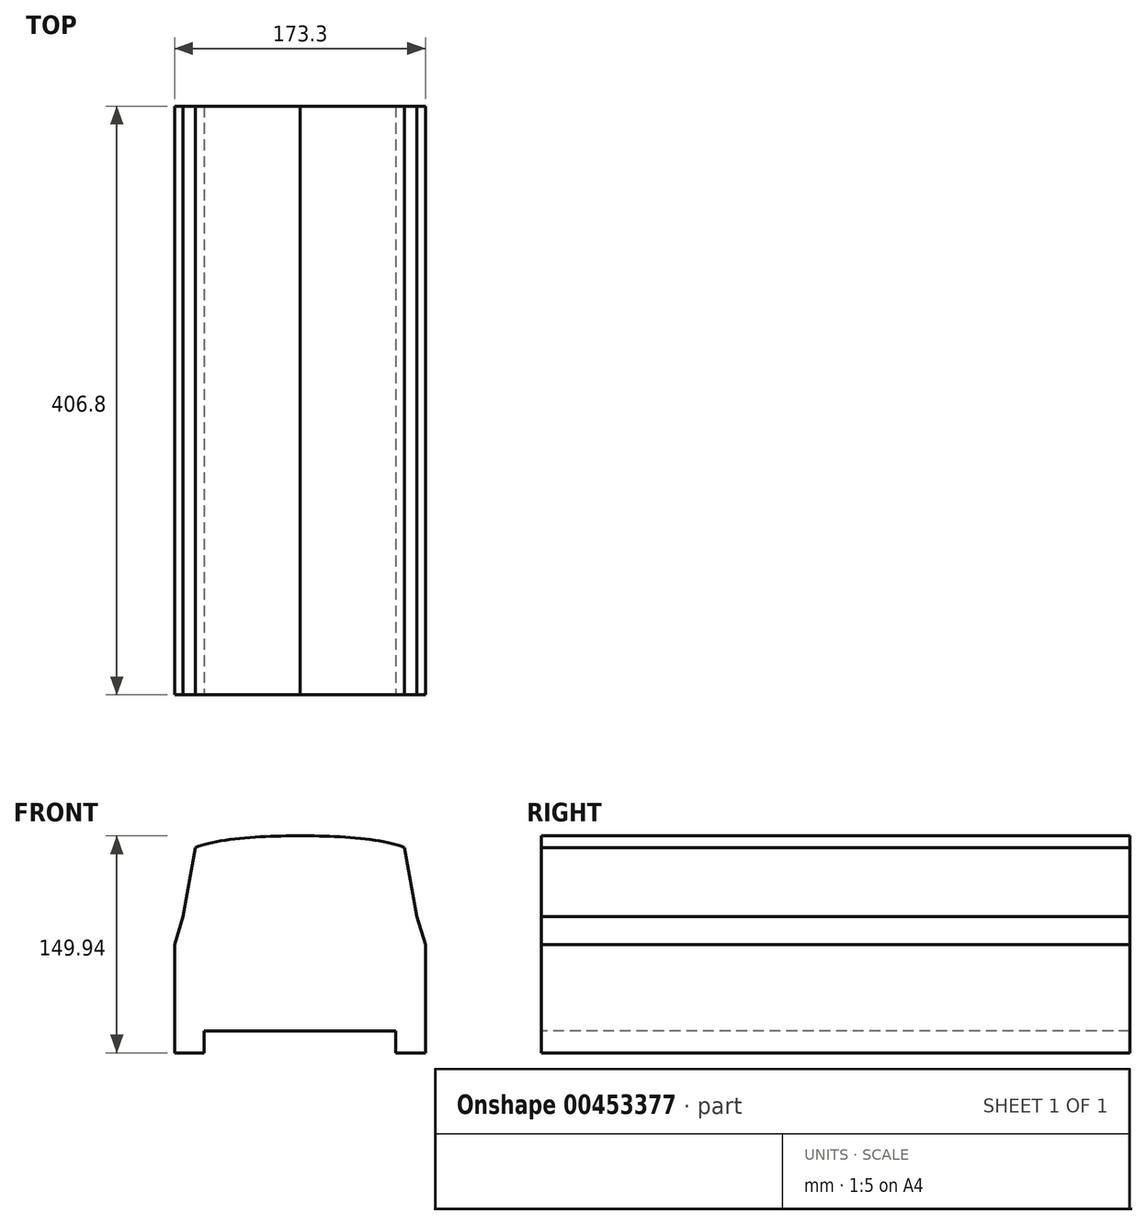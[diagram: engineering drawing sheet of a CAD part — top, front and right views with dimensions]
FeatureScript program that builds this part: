
annotation { "Feature Type Name" : "Feature", "Feature Type Description" : "" }
export const myFeature = defineFeature(function(context is Context, id is Id, definition is map)
    precondition{}
    {
        {
            var Q0;
            Q0=qCreatedBy(makeId("Front.planeOp"),FACE);
            var sketch = newSketch(context, id + "F0", { "sketchPlane" : qUnion([Q0])});
            skLineSegment(sketch, "E0.bottom", {"start": v(66.15, -74.64) * mm, "end": v(86.65, -74.64) * mm});
            skLineSegment(sketch, "E0.left", {"start": v(0, -59.64) * mm, "end": v(0, 75.26) * mm});
            skLineSegment(sketch, "E0.right", {"start": v(86.65, -74.64) * mm, "end": v(86.65, 0.31) * mm});
            skLineSegment(sketch, "E1.bottom", {"start": v(86.65, -74.64) * mm, "end": v(66.15, -74.64) * mm});
            skLineSegment(sketch, "E1.top", {"start": v(86.65, -59.64) * mm, "end": v(66.15, -59.64) * mm});
            skLineSegment(sketch, "E1.left", {"start": v(86.65, -74.64) * mm, "end": v(86.65, -59.64) * mm});
            skLineSegment(sketch, "E1.right", {"start": v(66.15, -74.64) * mm, "end": v(66.15, -59.64) * mm});
            skLineSegment(sketch, "E2", {"start": v(86.65, -59.64) * mm, "end": v(0, -59.64) * mm});
            skPoint(sketch, "E3.orphan", {"position": v(0, -74.64) * mm});
            skLineSegment(sketch, "E4", {"start": v(86.65, 0.31) * mm, "end": v(80.78, 19.68) * mm});
            skLineSegment(sketch, "E5", {"start": v(80.78, 19.68) * mm, "end": v(72.27, 67.32) * mm});
            skFitSpline(sketch, "E6", {"points": [v(72.27, 67.32) * mm, v(0, 75.26) * mm], "startDerivative": vector(-41.57, 18.23) * mm, "endDerivative": vector(-72.2, -1) * mm});
            skLineSegment(sketch, "E7", {"start": v(86.65, 0.31) * mm, "end": v(86.65, -59.64) * mm});
            skPoint(sketch, "E0.top.end.orphan", {"position": v(86.65, 75.26) * mm});
            skLineSegment(sketch, "E8", {"start": v(82.19, -59.64) * mm, "end": v(86.65, -52.38) * mm});
            skFitSpline(sketch, "E9.MirrorCS", {"points": [v(-72.27, 67.32) * mm, v(0, 75.26) * mm], "startDerivative": vector(41.57, 18.23) * mm, "endDerivative": vector(72.2, -1) * mm});
            skLineSegment(sketch, "E10.MirrorCS", {"start": v(-80.78, 19.68) * mm, "end": v(-72.27, 67.32) * mm});
            skLineSegment(sketch, "E11.MirrorCS", {"start": v(-86.65, 0.31) * mm, "end": v(-86.65, -59.64) * mm});
            skLineSegment(sketch, "E12.MirrorCS", {"start": v(-86.65, 0.31) * mm, "end": v(-80.78, 19.68) * mm});
            skLineSegment(sketch, "E13.MirrorCS", {"start": v(-82.19, -59.64) * mm, "end": v(-86.65, -52.38) * mm});
            skLineSegment(sketch, "E14.MirrorCS", {"start": v(-86.65, -74.64) * mm, "end": v(-86.65, -59.64) * mm});
            skLineSegment(sketch, "E15.MirrorCS", {"start": v(-86.65, -74.64) * mm, "end": v(-66.15, -74.64) * mm});
            skLineSegment(sketch, "E16.MirrorCS", {"start": v(-66.15, -74.64) * mm, "end": v(-66.15, -59.64) * mm});
            skLineSegment(sketch, "E17.MirrorCS", {"start": v(-86.65, -59.64) * mm, "end": v(0, -59.64) * mm});
            skSolve(sketch);
        }
        {
            var Q0;
            Q0 = qSketchRegion(id + "F0", true);
            extrude(context, id + "F1", {"entities" : qUnion([Q0]), "oppositeDirection" : true, "depth" : 406.8 * mm});
        }
    });
